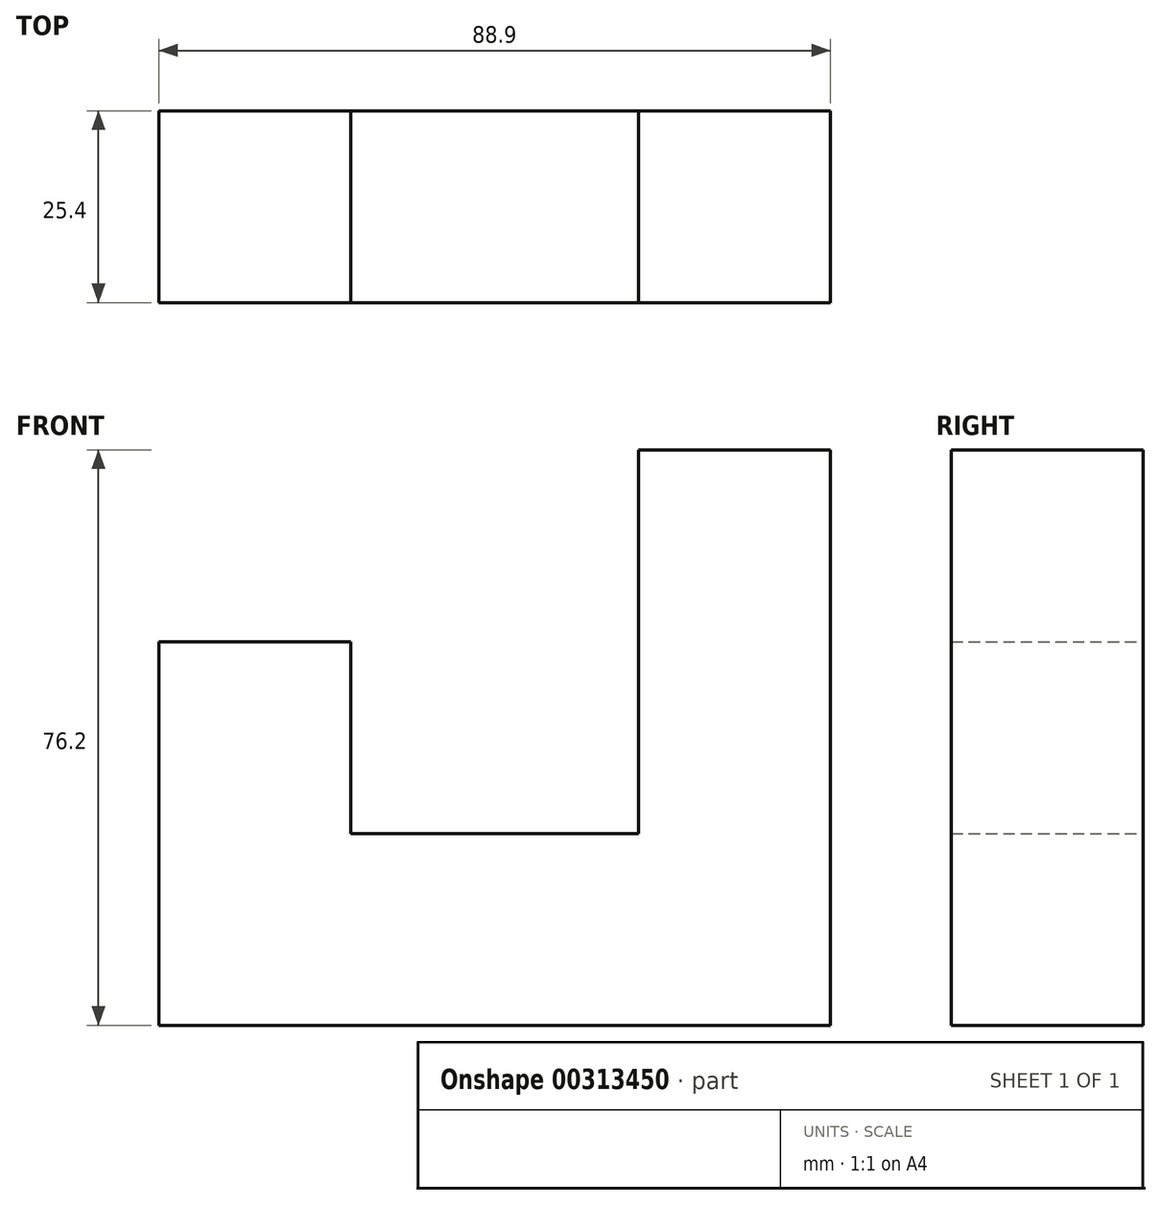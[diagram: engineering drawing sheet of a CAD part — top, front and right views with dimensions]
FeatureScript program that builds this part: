
annotation { "Feature Type Name" : "Feature", "Feature Type Description" : "" }
export const myFeature = defineFeature(function(context is Context, id is Id, definition is map)
    precondition{}
    {
        {
            var Q0;
            Q0=qCreatedBy(makeId("Front.planeOp"),FACE);
            var sketch = newSketch(context, id + "F0", { "sketchPlane" : qUnion([Q0])});
            skLineSegment(sketch, "E0", {"start": v(-57.83, -66.39) * mm, "end": v(31.07, -66.39) * mm});
            skLineSegment(sketch, "E1", {"start": v(31.07, -66.39) * mm, "end": v(31.07, 9.81) * mm});
            skLineSegment(sketch, "E2", {"start": v(31.07, 9.81) * mm, "end": v(5.67, 9.81) * mm});
            skLineSegment(sketch, "E3", {"start": v(5.67, 9.81) * mm, "end": v(5.67, -40.99) * mm});
            skLineSegment(sketch, "E4", {"start": v(5.67, -40.99) * mm, "end": v(-32.43, -40.99) * mm});
            skLineSegment(sketch, "E5", {"start": v(-32.43, -40.99) * mm, "end": v(-32.43, -15.59) * mm});
            skLineSegment(sketch, "E6", {"start": v(-32.43, -15.59) * mm, "end": v(-57.83, -15.59) * mm});
            skLineSegment(sketch, "E7", {"start": v(-57.83, -15.59) * mm, "end": v(-57.83, -66.39) * mm});
            skSolve(sketch);
        }
        {
            var Q0;
            Q0=makeQuery(id+"F0.imprint","IMPRINT",FACE,{"disambiguationData":[TD([[makeQuery(id+"F0.imprint","IMPRINT",EDGE,{"derivedFrom":sQuery(id+"F0.wireOp",EDGE,"E0")}),1.0]])]});
            extrude(context, id + "F1", {"entities" : qUnion([Q0]), "depth" : 25.4 * mm});
        }
    });
